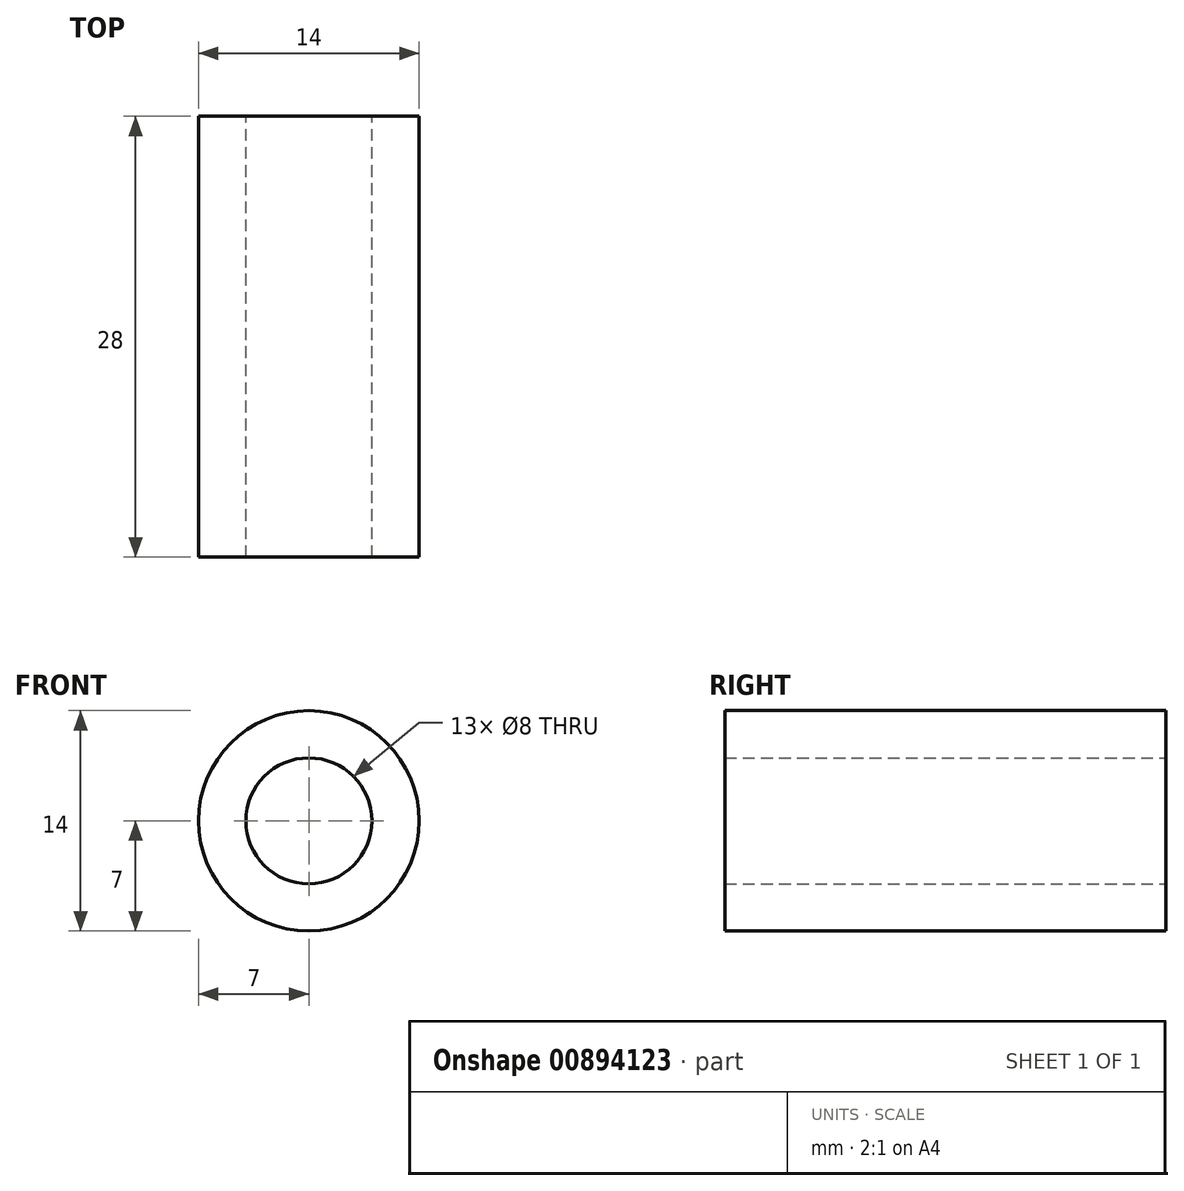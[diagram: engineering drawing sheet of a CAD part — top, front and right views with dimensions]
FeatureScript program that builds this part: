
annotation { "Feature Type Name" : "Feature", "Feature Type Description" : "" }
export const myFeature = defineFeature(function(context is Context, id is Id, definition is map)
    precondition{}
    {
        {
            var Q0;
            Q0=qCreatedBy(makeId("Front.planeOp"),FACE);
            var sketch = newSketch(context, id + "F0", { "sketchPlane" : qUnion([Q0])});
            skCircle(sketch, "E0", {"center": v(0, 0) * mm, "radius": 7 * mm});
            skCircle(sketch, "E1", {"center": v(0, 0) * mm, "radius": 4 * mm});
            skSolve(sketch);
        }
        {
            var Q0;
            Q0 = qSketchRegion(id + "F0", true);
            extrude(context, id + "F1", {"entities" : qUnion([Q0]), "depth" : 28 * mm, "offsetDistance" : 25 * mm});
        }
    });
